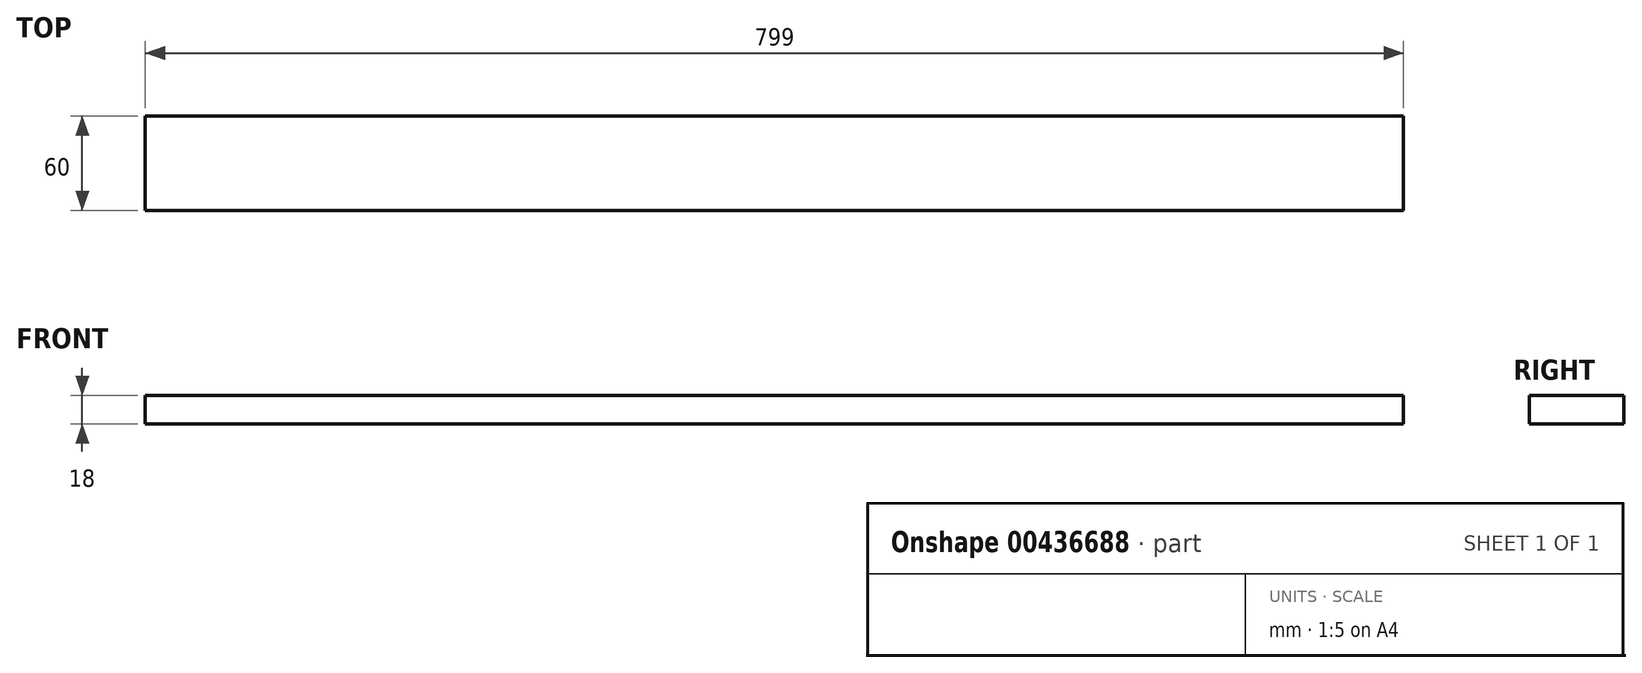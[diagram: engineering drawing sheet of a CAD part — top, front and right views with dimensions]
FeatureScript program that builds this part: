
annotation { "Feature Type Name" : "Feature", "Feature Type Description" : "" }
export const myFeature = defineFeature(function(context is Context, id is Id, definition is map)
    precondition{}
    {
        {
            var Q0;
            Q0=qCreatedBy(makeId("Right.planeOp"),FACE);
            var sketch = newSketch(context, id + "F0", { "sketchPlane" : qUnion([Q0])});
            skLineSegment(sketch, "E0.bottom", {"start": v(30, 9) * mm, "end": v(-30, 9) * mm});
            skLineSegment(sketch, "E0.top", {"start": v(30, -9) * mm, "end": v(-30, -9) * mm});
            skLineSegment(sketch, "E0.left", {"start": v(30, 9) * mm, "end": v(30, -9) * mm});
            skLineSegment(sketch, "E0.right", {"start": v(-30, 9) * mm, "end": v(-30, -9) * mm});
            skPoint(sketch, "E0.middle", {"position": v(0, 0) * mm});
            skSolve(sketch);
        }
        {
            var Q0;
            Q0=qSketchRegion(id+"F0",true);
            extrude(context, id + "F1", {"entities" : qUnion([Q0]), "depth" : 799 * mm});
        }
    });
